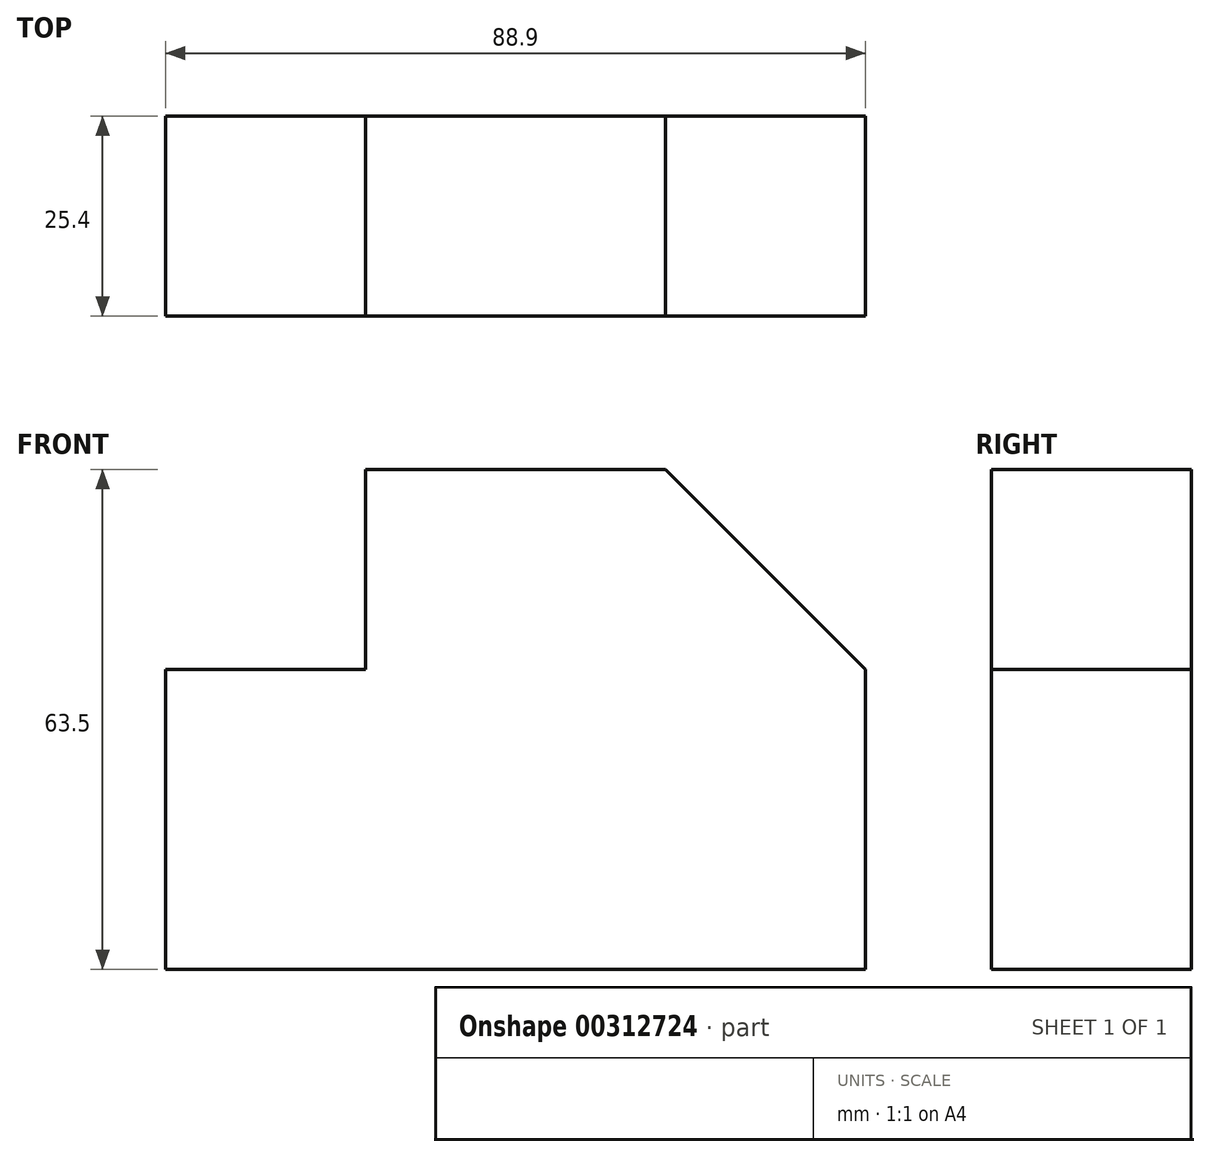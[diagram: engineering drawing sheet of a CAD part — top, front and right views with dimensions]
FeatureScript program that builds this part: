
annotation { "Feature Type Name" : "Feature", "Feature Type Description" : "" }
export const myFeature = defineFeature(function(context is Context, id is Id, definition is map)
    precondition{}
    {
        {
            var Q0;
            Q0=qCreatedBy(makeId("Front.planeOp"),FACE);
            var sketch = newSketch(context, id + "F0", { "sketchPlane" : qUnion([Q0])});
            skLineSegment(sketch, "E0", {"start": v(-51.83, 17.94) * mm, "end": v(-51.83, -20.16) * mm});
            skLineSegment(sketch, "E1", {"start": v(-51.83, -20.16) * mm, "end": v(37.07, -20.16) * mm});
            skLineSegment(sketch, "E2", {"start": v(37.07, -20.16) * mm, "end": v(37.07, 17.94) * mm});
            skLineSegment(sketch, "E3", {"start": v(-51.83, 17.94) * mm, "end": v(-26.43, 17.94) * mm});
            skLineSegment(sketch, "E4", {"start": v(-26.43, 17.94) * mm, "end": v(-26.43, 43.34) * mm});
            skLineSegment(sketch, "E5", {"start": v(-26.43, 43.34) * mm, "end": v(11.67, 43.34) * mm});
            skLineSegment(sketch, "E6", {"start": v(11.67, 43.34) * mm, "end": v(37.07, 17.94) * mm});
            skSolve(sketch);
        }
        {
            var Q0;
            Q0=makeQuery(id+"F0.imprint","IMPRINT",FACE,{"disambiguationData":[TD([[makeQuery(id+"F0.imprint","IMPRINT",EDGE,{"derivedFrom":sQuery(id+"F0.wireOp",EDGE,"E0")}),1.0]])]});
            extrude(context, id + "F1", {"entities" : qUnion([Q0]), "depth" : 25.4 * mm});
        }
    });
